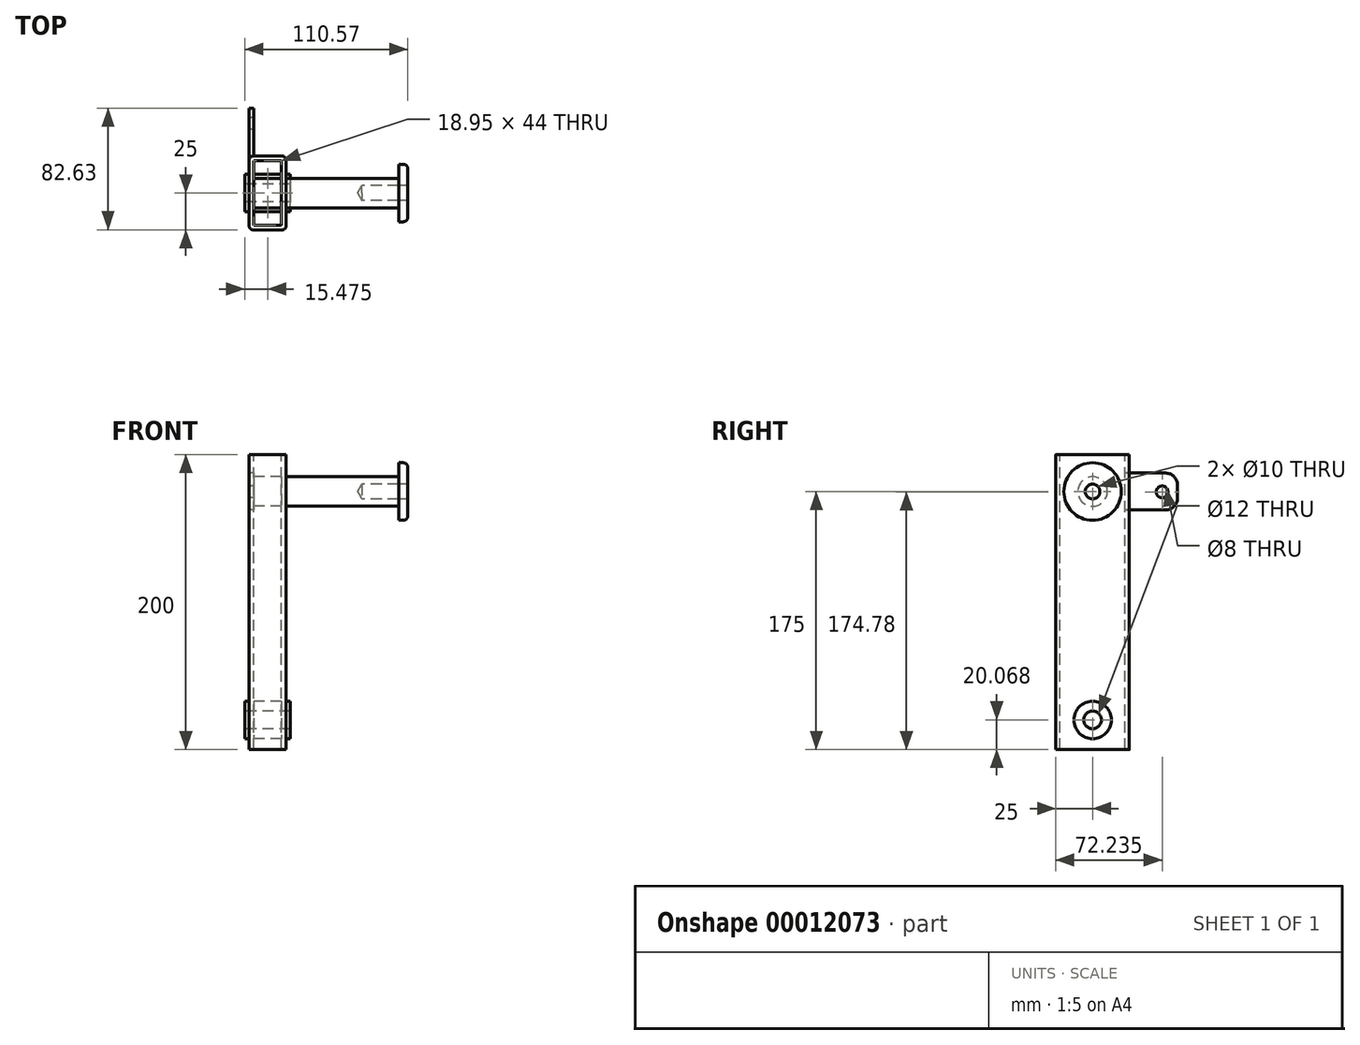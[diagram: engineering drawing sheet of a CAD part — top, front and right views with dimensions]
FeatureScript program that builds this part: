
annotation { "Feature Type Name" : "Feature", "Feature Type Description" : "" }
export const myFeature = defineFeature(function(context is Context, id is Id, definition is map)
    precondition{}
    {
        {
            var Q0;
            Q0=qCreatedBy(makeId("Front.planeOp"),FACE);
            var sketch = newSketch(context, id + "F0", { "sketchPlane" : qUnion([Q0])});
            skLineSegment(sketch, "E0", {"start": v(-25, 0) * mm, "end": v(48.61, 0) * mm});
            skLineSegment(sketch, "E1", {"start": v(-25, 10) * mm, "end": v(76.5, 10) * mm});
            skLineSegment(sketch, "E2", {"start": v(76.5, 10) * mm, "end": v(76.5, 5) * mm});
            skLineSegment(sketch, "E3", {"start": v(76.6, 5) * mm, "end": v(76.6, 19.51) * mm});
            skLineSegment(sketch, "E4", {"start": v(76.6, 19.51) * mm, "end": v(79.62, 19.51) * mm});
            skLineSegment(sketch, "E5", {"start": v(82.62, 16.51) * mm, "end": v(82.62, 5) * mm});
            skLineSegment(sketch, "E6", {"start": v(82.62, 5) * mm, "end": v(76.6, 5) * mm});
            skLineSegment(sketch, "E7", {"start": v(51.5, 5) * mm, "end": v(48.61, 0) * mm});
            skPoint(sketch, "E8.visualSharp", {"position": v(82.62, 19.51) * mm});
            skArc(sketch, "E8.filletArc", {"start": v(82.62, 16.51) * mm, "mid": v(81.74, 18.63) * mm, "end": v(79.62, 19.51) * mm});
            skPoint(sketch, "E9.orphan", {"position": v(76.6, 0) * mm});
            skPoint(sketch, "E10.orphan", {"position": v(76.5, 0) * mm});
            skLineSegment(sketch, "E11.trimOffspring", {"start": v(76.5, 5) * mm, "end": v(51.5, 5) * mm});
            skLineSegment(sketch, "E12", {"start": v(-25, 10) * mm, "end": v(-25, 0) * mm});
            skSolve(sketch);
        }
        {
            var Q0;
            Q0 = qSketchRegion(id + "F0", true);
            var Q1;
            Q1=sQuery(id+"F0.wireOp",EDGE,"E0");
            revolve(context, id + "F1", {"entities" : qUnion([Q0]), "axis" : qUnion([Q1]), "revolveType" : RevolveType.FULL});
        }
        {
            var Q0;
            Q0=qCreatedBy(makeId("Top.planeOp"),FACE);
            cPlane(context, id + "F2", {"entities" : qUnion([Q0]), "cplaneType" : CPlaneType.OFFSET, "offset" : 25 * mm, "width" : 150 * mm, "height" : 150 * mm});
        }
        {
            var Q0;
            Q0=qCreatedBy(id+"F2.planeOp",FACE);
            var sketch = newSketch(context, id + "F3", { "sketchPlane" : qUnion([Q0])});
            skLineSegment(sketch, "E13.top", {"start": v(-22.45, -25) * mm, "end": v(-2.5, -25) * mm});
            skLineSegment(sketch, "E13.left", {"start": v(-24.95, 22.5) * mm, "end": v(-24.95, -22.5) * mm});
            skLineSegment(sketch, "E13.right", {"start": v(0, 22.5) * mm, "end": v(0, -22.5) * mm});
            skLineSegment(sketch, "E14", {"start": v(-22.45, 25) * mm, "end": v(-2.5, 25) * mm});
            skPoint(sketch, "E13.bottom.start.orphan", {"position": v(-24.95, 0) * mm});
            skPoint(sketch, "E15.visualSharp", {"position": v(-24.95, -25) * mm});
            skArc(sketch, "E15.filletArc", {"start": v(-24.95, -22.5) * mm, "mid": v(-24.22, -24.27) * mm, "end": v(-22.45, -25) * mm});
            skPoint(sketch, "E16.visualSharp", {"position": v(0, -25) * mm});
            skArc(sketch, "E16.filletArc", {"start": v(-2.5, -25) * mm, "mid": v(-0.73, -24.27) * mm, "end": v(0, -22.5) * mm});
            skPoint(sketch, "E17.visualSharp", {"position": v(0, 25) * mm});
            skArc(sketch, "E17.filletArc", {"start": v(0, 22.5) * mm, "mid": v(-0.73, 24.27) * mm, "end": v(-2.5, 25) * mm});
            skPoint(sketch, "E18.visualSharp", {"position": v(-24.95, 25) * mm});
            skArc(sketch, "E18.filletArc", {"start": v(-22.45, 25) * mm, "mid": v(-24.22, 24.27) * mm, "end": v(-24.95, 22.5) * mm});
            skLineSegment(sketch, "E19.0", {"start": v(-21.95, -22) * mm, "end": v(-3, -22) * mm});
            skLineSegment(sketch, "E19.1", {"start": v(-21.95, 22) * mm, "end": v(-21.95, -22) * mm});
            skLineSegment(sketch, "E19.2", {"start": v(-21.95, 22) * mm, "end": v(-3, 22) * mm});
            skLineSegment(sketch, "E19.3", {"start": v(-3, 22) * mm, "end": v(-3, -22) * mm});
            skSolve(sketch);
        }
        {
            var Q0;
            Q0 = qSketchRegion(id + "F3", true);
            extrude(context, id + "F4", {"entities" : qUnion([Q0]), "operationType" : NewBodyOperationType.ADD, "oppositeDirection" : true, "depth" : 200 * mm});
        }
        {
            var Q0;
            Q0=makeQuery(id+"F4.opExtrude","SWEPT_FACE",FACE,{"disambiguationData":[OSD([sQuery(id+"F3.wireOp",EDGE,"E13.right")])]});
            var sketch = newSketch(context, id + "F5", { "sketchPlane" : qUnion([Q0])});
            skCircle(sketch, "E20", {"center": v(0, -154.93) * mm, "radius": 12.7 * mm});
            skPoint(sketch, "E20.centerSnap0", {"position": v(0, -175) * mm});
            skSolve(sketch);
        }
        {
            var Q0;
            Q0 = qSketchRegion(id + "F5", true);
            extrude(context, id + "F6", {"entities" : qUnion([Q0]), "operationType" : NewBodyOperationType.REMOVE, "endBound" : BoundingType.THROUGH_ALL, "oppositeDirection" : true, "depth" : 25 * mm});
        }
        {
            var Q0;
            Q0=makeQuery(id+"F4.opExtrude","SWEPT_FACE",FACE,{"disambiguationData":[OSD([sQuery(id+"F3.wireOp",EDGE,"E13.left")])]});
            var sketch = newSketch(context, id + "F7", { "sketchPlane" : qUnion([Q0])});
            skCircle(sketch, "E21", {"center": v(0, -154.93) * mm, "radius": 12.7 * mm});
            skCircle(sketch, "E22", {"center": v(0, -154.93) * mm, "radius": 6 * mm});
            skSolve(sketch);
        }
        {
            var Q0;
            Q0 = qSketchRegion(id + "F7", true);
            extrude(context, id + "F8", {"entities" : qUnion([Q0]), "operationType" : NewBodyOperationType.ADD, "oppositeDirection" : true, "depth" : 28 * mm, "hasSecondDirection" : true, "secondDirectionOppositeDirection" : false, "secondDirectionDepth" : 3 * mm});
        }
        {
            var Q0;
            Q0=makeQuery(id+"F4.opExtrude","SWEPT_FACE",FACE,{"disambiguationData":[OSD([sQuery(id+"F3.wireOp",EDGE,"E13.left")])]});
            var sketch = newSketch(context, id + "F9", { "sketchPlane" : qUnion([Q0])});
            skLineSegment(sketch, "E23.bottom", {"start": v(-22.5, 12.5) * mm, "end": v(-49.63, 12.5) * mm});
            skLineSegment(sketch, "E23.top", {"start": v(-22.5, -12.5) * mm, "end": v(-49.63, -12.5) * mm});
            skLineSegment(sketch, "E23.left", {"start": v(-22.5, 12.5) * mm, "end": v(-22.5, -12.5) * mm});
            skLineSegment(sketch, "E23.right", {"start": v(-57.63, 4.5) * mm, "end": v(-57.63, -4.5) * mm});
            skPoint(sketch, "E24.visualSharp", {"position": v(-57.63, 12.5) * mm});
            skArc(sketch, "E24.filletArc", {"start": v(-49.63, 12.5) * mm, "mid": v(-55.29, 10.16) * mm, "end": v(-57.63, 4.5) * mm});
            skPoint(sketch, "E25.visualSharp", {"position": v(-57.63, -12.5) * mm});
            skArc(sketch, "E25.filletArc", {"start": v(-57.63, -4.5) * mm, "mid": v(-55.29, -10.16) * mm, "end": v(-49.63, -12.5) * mm});
            skCircle(sketch, "E26", {"center": v(-47.23, -0.22) * mm, "radius": 4 * mm});
            skSolve(sketch);
        }
        {
            var Q0;
            Q0 = qSketchRegion(id + "F9", true);
            extrude(context, id + "F10", {"entities" : qUnion([Q0]), "operationType" : NewBodyOperationType.ADD, "oppositeDirection" : true, "depth" : 3 * mm});
        }
    });
